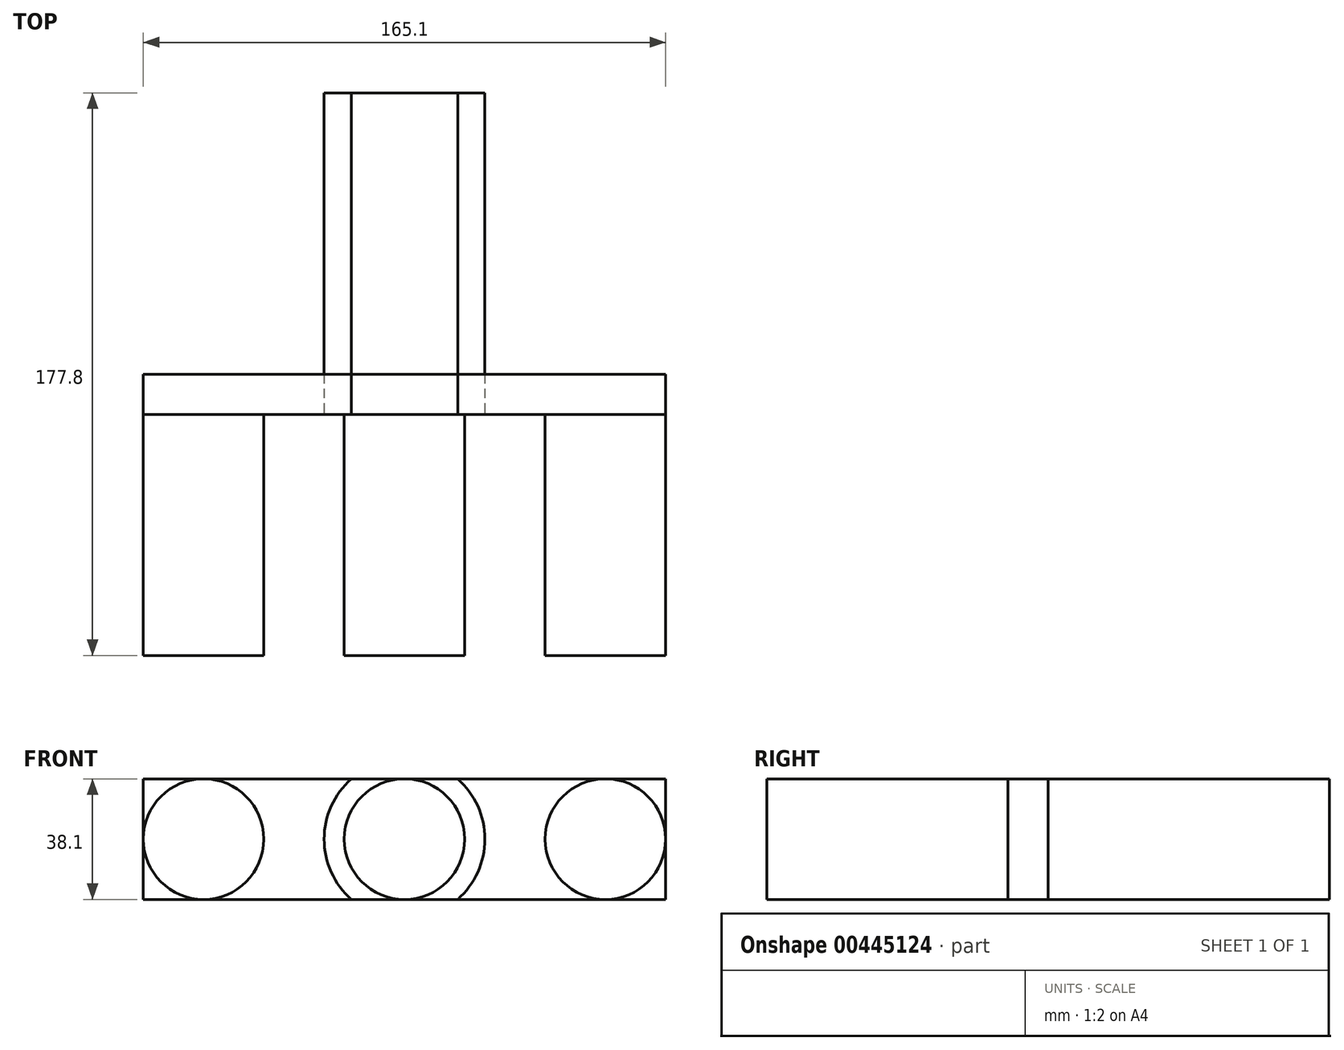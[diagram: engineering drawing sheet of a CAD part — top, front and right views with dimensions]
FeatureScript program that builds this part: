
annotation { "Feature Type Name" : "Feature", "Feature Type Description" : "" }
export const myFeature = defineFeature(function(context is Context, id is Id, definition is map)
    precondition{}
    {
        {
            var Q0;
            Q0=qCreatedBy(makeId("Front.planeOp"),FACE);
            var sketch = newSketch(context, id + "F0", { "sketchPlane" : qUnion([Q0])});
            skCircle(sketch, "E0", {"center": v(-63.5, 0) * mm, "radius": 19.05 * mm});
            skCircle(sketch, "E1", {"center": v(0, 0) * mm, "radius": 19.05 * mm});
            skCircle(sketch, "E2", {"center": v(63.5, 0) * mm, "radius": 19.05 * mm});
            skLineSegment(sketch, "E3", {"start": v(-63.5, 0) * mm, "end": v(0, 0) * mm});
            skLineSegment(sketch, "E4", {"start": v(0, 0) * mm, "end": v(63.5, 0) * mm});
            skLineSegment(sketch, "E5.bottom", {"start": v(82.55, -19.05) * mm, "end": v(-82.55, -19.05) * mm});
            skLineSegment(sketch, "E5.top", {"start": v(82.55, 19.05) * mm, "end": v(-82.55, 19.05) * mm});
            skLineSegment(sketch, "E5.left", {"start": v(82.55, -19.05) * mm, "end": v(82.55, 19.05) * mm});
            skLineSegment(sketch, "E5.right", {"start": v(-82.55, -19.05) * mm, "end": v(-82.55, 19.05) * mm});
            skCircle(sketch, "E6", {"center": v(0, 0) * mm, "radius": 25.4 * mm});
            skSolve(sketch);
        }
        {
            var Q0;
            {var subQ0=sQuery(id+"F0.wireOp",EDGE,"E0");var subQ1=makeQuery(id+"F0.imprint","INTERSECT",VERTEX,{"derivedFrom":[subQ0,sQuery(id+"F0.wireOp",EDGE,"E5.top")]});Q0=makeQuery(id+"F0.imprint","IMPRINT",FACE,{"disambiguationData":[TD([[makeQuery(id+"F0.imprint","IMPRINT",EDGE,{"disambiguationData":[TD([[subQ1,1.0]])],"derivedFrom":subQ0}),1.0]])]});}
            var Q1;
            {var subQ0=sQuery(id+"F0.wireOp",EDGE,"E2");var subQ1=makeQuery(id+"F0.imprint","INTERSECT",VERTEX,{"derivedFrom":[subQ0,sQuery(id+"F0.wireOp",EDGE,"E5.top")]});Q1=makeQuery(id+"F0.imprint","IMPRINT",FACE,{"disambiguationData":[TD([[makeQuery(id+"F0.imprint","IMPRINT",EDGE,{"disambiguationData":[TD([[subQ1,1.0]])],"derivedFrom":subQ0}),1.0]])]});}
            var Q2;
            {var subQ0=sQuery(id+"F0.wireOp",EDGE,"E1");var subQ1=makeQuery(id+"F0.imprint","INTERSECT",VERTEX,{"derivedFrom":[subQ0,sQuery(id+"F0.wireOp",EDGE,"E5.top")]});Q2=makeQuery(id+"F0.imprint","IMPRINT",FACE,{"disambiguationData":[TD([[makeQuery(id+"F0.imprint","IMPRINT",EDGE,{"disambiguationData":[TD([[subQ1,1.0]])],"derivedFrom":subQ0}),1.0]])]});}
            var Q3;
            {var subQ0=sQuery(id+"F0.wireOp",EDGE,"E3");var subQ1=sQuery(id+"F0.wireOp",EDGE,"E1");var subQ2=makeQuery(id+"F0.imprint","INTERSECT",VERTEX,{"derivedFrom":[subQ1,subQ0]});Q3=makeQuery(id+"F0.imprint","IMPRINT",FACE,{"disambiguationData":[TD([[makeQuery(id+"F0.imprint","IMPRINT",EDGE,{"disambiguationData":[TD([[subQ2,-1.0]])],"derivedFrom":subQ1}),1.0]])]});}
            extrude(context, id + "F1", {"entities" : qUnion([Q0, Q1, Q2, Q3]), "depth" : 76.2 * mm});
        }
        {
            var Q0;
            {var subQ0=sQuery(id+"F0.wireOp",EDGE,"E5.top");var subQ1=sQuery(id+"F0.wireOp",EDGE,"E0");var subQ2=makeQuery(id+"F0.imprint","INTERSECT",VERTEX,{"derivedFrom":[subQ1,subQ0]});Q0=makeQuery(id+"F0.imprint","IMPRINT",FACE,{"disambiguationData":[TD([[makeQuery(id+"F0.imprint","IMPRINT",EDGE,{"disambiguationData":[TD([[subQ2,-1.0]])],"derivedFrom":subQ1}),-1.0]])]});}
            var Q1;
            {var subQ0=sQuery(id+"F0.wireOp",EDGE,"E5.right");var subQ1=sQuery(id+"F0.wireOp",EDGE,"E0");var subQ2=makeQuery(id+"F0.imprint","INTERSECT",VERTEX,{"derivedFrom":[subQ1,subQ0]});Q1=makeQuery(id+"F0.imprint","IMPRINT",FACE,{"disambiguationData":[TD([[makeQuery(id+"F0.imprint","IMPRINT",EDGE,{"disambiguationData":[TD([[subQ2,-1.0]])],"derivedFrom":subQ1}),-1.0]])]});}
            var Q2;
            {var subQ0=sQuery(id+"F0.wireOp",EDGE,"E5.top");var subQ1=sQuery(id+"F0.wireOp",EDGE,"E2");var subQ2=makeQuery(id+"F0.imprint","INTERSECT",VERTEX,{"derivedFrom":[subQ1,subQ0]});Q2=makeQuery(id+"F0.imprint","IMPRINT",FACE,{"disambiguationData":[TD([[makeQuery(id+"F0.imprint","IMPRINT",EDGE,{"disambiguationData":[TD([[subQ2,1.0]])],"derivedFrom":subQ1}),-1.0]])]});}
            var Q3;
            {var subQ0=sQuery(id+"F0.wireOp",EDGE,"E5.left");var subQ1=sQuery(id+"F0.wireOp",EDGE,"E2");var subQ2=makeQuery(id+"F0.imprint","INTERSECT",VERTEX,{"derivedFrom":[subQ1,subQ0]});Q3=makeQuery(id+"F0.imprint","IMPRINT",FACE,{"disambiguationData":[TD([[makeQuery(id+"F0.imprint","IMPRINT",EDGE,{"disambiguationData":[TD([[subQ2,1.0]])],"derivedFrom":subQ1}),-1.0]])]});}
            var Q4;
            {var subQ0=sQuery(id+"F0.wireOp",EDGE,"E5.top");var subQ1=sQuery(id+"F0.wireOp",EDGE,"E0");var subQ2=makeQuery(id+"F0.imprint","INTERSECT",VERTEX,{"derivedFrom":[subQ1,subQ0]});Q4=makeQuery(id+"F0.imprint","IMPRINT",FACE,{"disambiguationData":[TD([[makeQuery(id+"F0.imprint","IMPRINT",EDGE,{"disambiguationData":[TD([[subQ2,1.0]])],"derivedFrom":subQ1}),-1.0]])]});}
            var Q5;
            {var subQ0=sQuery(id+"F0.wireOp",EDGE,"E3");var subQ1=sQuery(id+"F0.wireOp",EDGE,"E0");var subQ2=makeQuery(id+"F0.imprint","INTERSECT",VERTEX,{"derivedFrom":[subQ1,subQ0]});Q5=makeQuery(id+"F0.imprint","IMPRINT",FACE,{"disambiguationData":[TD([[makeQuery(id+"F0.imprint","IMPRINT",EDGE,{"disambiguationData":[TD([[subQ2,1.0]])],"derivedFrom":subQ1}),-1.0]])]});}
            var Q6;
            {var subQ0=sQuery(id+"F0.wireOp",EDGE,"E5.top");var subQ1=sQuery(id+"F0.wireOp",EDGE,"E2");var subQ2=makeQuery(id+"F0.imprint","INTERSECT",VERTEX,{"derivedFrom":[subQ1,subQ0]});Q6=makeQuery(id+"F0.imprint","IMPRINT",FACE,{"disambiguationData":[TD([[makeQuery(id+"F0.imprint","IMPRINT",EDGE,{"disambiguationData":[TD([[subQ2,-1.0]])],"derivedFrom":subQ1}),-1.0]])]});}
            var Q7;
            {var subQ0=sQuery(id+"F0.wireOp",EDGE,"E4");var subQ1=sQuery(id+"F0.wireOp",EDGE,"E2");var subQ2=makeQuery(id+"F0.imprint","INTERSECT",VERTEX,{"derivedFrom":[subQ1,subQ0]});Q7=makeQuery(id+"F0.imprint","IMPRINT",FACE,{"disambiguationData":[TD([[makeQuery(id+"F0.imprint","IMPRINT",EDGE,{"disambiguationData":[TD([[subQ2,-1.0]])],"derivedFrom":subQ1}),-1.0]])]});}
            var Q8;
            {var subQ0=sQuery(id+"F0.wireOp",EDGE,"E5.top");var subQ1=sQuery(id+"F0.wireOp",EDGE,"E1");var subQ2=makeQuery(id+"F0.imprint","INTERSECT",VERTEX,{"derivedFrom":[subQ1,subQ0]});Q8=makeQuery(id+"F0.imprint","IMPRINT",FACE,{"disambiguationData":[TD([[makeQuery(id+"F0.imprint","IMPRINT",EDGE,{"disambiguationData":[TD([[subQ2,1.0]])],"derivedFrom":subQ1}),-1.0]])]});}
            var Q9;
            {var subQ0=sQuery(id+"F0.wireOp",EDGE,"E5.top");var subQ1=sQuery(id+"F0.wireOp",EDGE,"E1");var subQ2=makeQuery(id+"F0.imprint","INTERSECT",VERTEX,{"derivedFrom":[subQ1,subQ0]});Q9=makeQuery(id+"F0.imprint","IMPRINT",FACE,{"disambiguationData":[TD([[makeQuery(id+"F0.imprint","IMPRINT",EDGE,{"disambiguationData":[TD([[subQ2,-1.0]])],"derivedFrom":subQ1}),-1.0]])]});}
            var Q10;
            {var subQ0=sQuery(id+"F0.wireOp",EDGE,"E3");var subQ1=sQuery(id+"F0.wireOp",EDGE,"E1");var subQ2=makeQuery(id+"F0.imprint","INTERSECT",VERTEX,{"derivedFrom":[subQ1,subQ0]});Q10=makeQuery(id+"F0.imprint","IMPRINT",FACE,{"disambiguationData":[TD([[makeQuery(id+"F0.imprint","IMPRINT",EDGE,{"disambiguationData":[TD([[subQ2,-1.0]])],"derivedFrom":subQ1}),-1.0]])]});}
            var Q11;
            {var subQ0=sQuery(id+"F0.wireOp",EDGE,"E4");var subQ1=sQuery(id+"F0.wireOp",EDGE,"E1");var subQ2=makeQuery(id+"F0.imprint","INTERSECT",VERTEX,{"derivedFrom":[subQ1,subQ0]});Q11=makeQuery(id+"F0.imprint","IMPRINT",FACE,{"disambiguationData":[TD([[makeQuery(id+"F0.imprint","IMPRINT",EDGE,{"disambiguationData":[TD([[subQ2,1.0]])],"derivedFrom":subQ1}),-1.0]])]});}
            var Q12;
            {var subQ0=sQuery(id+"F0.wireOp",EDGE,"E0");var subQ1=makeQuery(id+"F0.imprint","INTERSECT",VERTEX,{"derivedFrom":[subQ0,sQuery(id+"F0.wireOp",EDGE,"E5.top")]});Q12=makeQuery(id+"F0.imprint","IMPRINT",FACE,{"disambiguationData":[TD([[makeQuery(id+"F0.imprint","IMPRINT",EDGE,{"disambiguationData":[TD([[subQ1,1.0]])],"derivedFrom":subQ0}),1.0]])]});}
            var Q13;
            {var subQ0=sQuery(id+"F0.wireOp",EDGE,"E1");var subQ1=makeQuery(id+"F0.imprint","INTERSECT",VERTEX,{"derivedFrom":[subQ0,sQuery(id+"F0.wireOp",EDGE,"E5.top")]});Q13=makeQuery(id+"F0.imprint","IMPRINT",FACE,{"disambiguationData":[TD([[makeQuery(id+"F0.imprint","IMPRINT",EDGE,{"disambiguationData":[TD([[subQ1,1.0]])],"derivedFrom":subQ0}),1.0]])]});}
            var Q14;
            {var subQ0=sQuery(id+"F0.wireOp",EDGE,"E2");var subQ1=makeQuery(id+"F0.imprint","INTERSECT",VERTEX,{"derivedFrom":[subQ0,sQuery(id+"F0.wireOp",EDGE,"E5.top")]});Q14=makeQuery(id+"F0.imprint","IMPRINT",FACE,{"disambiguationData":[TD([[makeQuery(id+"F0.imprint","IMPRINT",EDGE,{"disambiguationData":[TD([[subQ1,1.0]])],"derivedFrom":subQ0}),1.0]])]});}
            var Q15;
            {var subQ0=sQuery(id+"F0.wireOp",EDGE,"E3");var subQ1=sQuery(id+"F0.wireOp",EDGE,"E1");var subQ2=makeQuery(id+"F0.imprint","INTERSECT",VERTEX,{"derivedFrom":[subQ1,subQ0]});Q15=makeQuery(id+"F0.imprint","IMPRINT",FACE,{"disambiguationData":[TD([[makeQuery(id+"F0.imprint","IMPRINT",EDGE,{"disambiguationData":[TD([[subQ2,-1.0]])],"derivedFrom":subQ1}),1.0]])]});}
            extrude(context, id + "F2", {"entities" : qUnion([Q0, Q1, Q2, Q3, Q4, Q5, Q6, Q7, Q8, Q9, Q10, Q11, Q12, Q13, Q14, Q15]), "oppositeDirection" : true, "depth" : 12.7 * mm});
        }
        {
            var Q0;
            {var subQ0=sQuery(id+"F0.wireOp",EDGE,"E6");var subQ1=sQuery(id+"F0.wireOp",EDGE,"E5.top");var subQ2=makeQuery(id+"F0.imprint","INTERSECT",VERTEX,{"disambiguationData":[OD(0.0)],"derivedFrom":[subQ1,subQ0]});Q0=makeQuery(id+"F0.imprint","IMPRINT",FACE,{"disambiguationData":[TD([[makeQuery(id+"F0.imprint","IMPRINT",EDGE,{"disambiguationData":[TD([[subQ2,-1.0]])],"derivedFrom":subQ1}),-1.0]])]});}
            var Q1;
            {var subQ0=sQuery(id+"F0.wireOp",EDGE,"E5.top");var subQ1=sQuery(id+"F0.wireOp",EDGE,"E1");var subQ2=makeQuery(id+"F0.imprint","INTERSECT",VERTEX,{"derivedFrom":[subQ1,subQ0]});Q1=makeQuery(id+"F0.imprint","IMPRINT",FACE,{"disambiguationData":[TD([[makeQuery(id+"F0.imprint","IMPRINT",EDGE,{"disambiguationData":[TD([[subQ2,-1.0]])],"derivedFrom":subQ1}),-1.0]])]});}
            var Q2;
            {var subQ0=sQuery(id+"F0.wireOp",EDGE,"E5.top");var subQ1=sQuery(id+"F0.wireOp",EDGE,"E1");var subQ2=makeQuery(id+"F0.imprint","INTERSECT",VERTEX,{"derivedFrom":[subQ1,subQ0]});Q2=makeQuery(id+"F0.imprint","IMPRINT",FACE,{"disambiguationData":[TD([[makeQuery(id+"F0.imprint","IMPRINT",EDGE,{"disambiguationData":[TD([[subQ2,1.0]])],"derivedFrom":subQ1}),-1.0]])]});}
            var Q3;
            {var subQ0=sQuery(id+"F0.wireOp",EDGE,"E4");var subQ1=sQuery(id+"F0.wireOp",EDGE,"E1");var subQ2=makeQuery(id+"F0.imprint","INTERSECT",VERTEX,{"derivedFrom":[subQ1,subQ0]});Q3=makeQuery(id+"F0.imprint","IMPRINT",FACE,{"disambiguationData":[TD([[makeQuery(id+"F0.imprint","IMPRINT",EDGE,{"disambiguationData":[TD([[subQ2,1.0]])],"derivedFrom":subQ1}),-1.0]])]});}
            var Q4;
            {var subQ0=sQuery(id+"F0.wireOp",EDGE,"E6");var subQ1=sQuery(id+"F0.wireOp",EDGE,"E5.bottom");var subQ2=makeQuery(id+"F0.imprint","INTERSECT",VERTEX,{"disambiguationData":[OD(0.0)],"derivedFrom":[subQ1,subQ0]});Q4=makeQuery(id+"F0.imprint","IMPRINT",FACE,{"disambiguationData":[TD([[makeQuery(id+"F0.imprint","IMPRINT",EDGE,{"disambiguationData":[TD([[subQ2,-1.0]])],"derivedFrom":subQ1}),1.0]])]});}
            var Q5;
            {var subQ0=sQuery(id+"F0.wireOp",EDGE,"E3");var subQ1=sQuery(id+"F0.wireOp",EDGE,"E1");var subQ2=makeQuery(id+"F0.imprint","INTERSECT",VERTEX,{"derivedFrom":[subQ1,subQ0]});Q5=makeQuery(id+"F0.imprint","IMPRINT",FACE,{"disambiguationData":[TD([[makeQuery(id+"F0.imprint","IMPRINT",EDGE,{"disambiguationData":[TD([[subQ2,-1.0]])],"derivedFrom":subQ1}),-1.0]])]});}
            var Q6;
            {var subQ0=sQuery(id+"F0.wireOp",EDGE,"E1");var subQ1=makeQuery(id+"F0.imprint","INTERSECT",VERTEX,{"derivedFrom":[subQ0,sQuery(id+"F0.wireOp",EDGE,"E5.top")]});Q6=makeQuery(id+"F0.imprint","IMPRINT",FACE,{"disambiguationData":[TD([[makeQuery(id+"F0.imprint","IMPRINT",EDGE,{"disambiguationData":[TD([[subQ1,1.0]])],"derivedFrom":subQ0}),1.0]])]});}
            var Q7;
            {var subQ0=sQuery(id+"F0.wireOp",EDGE,"E3");var subQ1=sQuery(id+"F0.wireOp",EDGE,"E1");var subQ2=makeQuery(id+"F0.imprint","INTERSECT",VERTEX,{"derivedFrom":[subQ1,subQ0]});Q7=makeQuery(id+"F0.imprint","IMPRINT",FACE,{"disambiguationData":[TD([[makeQuery(id+"F0.imprint","IMPRINT",EDGE,{"disambiguationData":[TD([[subQ2,-1.0]])],"derivedFrom":subQ1}),1.0]])]});}
            extrude(context, id + "F3", {"entities" : qUnion([Q0, Q1, Q2, Q3, Q4, Q5, Q6, Q7]), "oppositeDirection" : true, "depth" : 101.6 * mm});
        }
    });
